# Revit family: Kompakt_WC_stojacy_z_deska_PVC_stal_szlachetna_matowa
name_source: partatom
category: Plumbing Fixtures
units: mm (PartAtom-declared; Revit-internal decimal feet)

## family parameters
Always vertical = Yes
Cut with Voids When Loaded = No
Host = Wall
Part Type = Normal
Room Calculation Point = No
Round Connector Dimension = Use Diameter
Shared = No

## types (1)
- UR2A
    Color / Kolor = Matowe (miska), biały (deska)
    Depth / Glebokosc = 620 mm  [stored 2.03412 ft]
    Description = Kompakt WC stojący to wykonany ze stali nierdzewnej model, charakteryzujący się bardzo dużą odpornością na uszkodzenia mechaniczne. Można wykorzystać go w toaletach, w których nie da się zamontować stelaża podtynkowego. W komplecie zawiera białą, uniwersalną deskę z tworzywa PVC. Łatwy w obsłudze i czyszczeniu WC kompakt to model wysokim stopniu wandaloodporności.
    Deska = PCV biały
    Height / Wysokosc = 680 mm  [stored 2.23097 ft]
    Manufacturer = FANECO.com
    Manufacturer code / Kod producenta = 5901764292005
    Material = Stal nierdzewna AISI 304
    Material finish / Wykonczenie = Stal nierdzewna 304 szczotkowana (miska), tworzywo PVC (deska)
    Product code / Kod produktu = UR2A
    Type Comments = KOMPAKT WC stojący z deską PVC stal szlachetna matowa
    URL = https://faneco.com
    Weight / Waga = 20.1 kg
    Width / Szerokosc = 370 mm  [stored 1.21391 ft]

note: [stored X ft] marks values corroborated as IEEE doubles in the binary element streams (Revit-internal decimal feet)

## geometry (parser evidence)
native form markers: Sweep x11
no freeform markers — native parametric forms only
